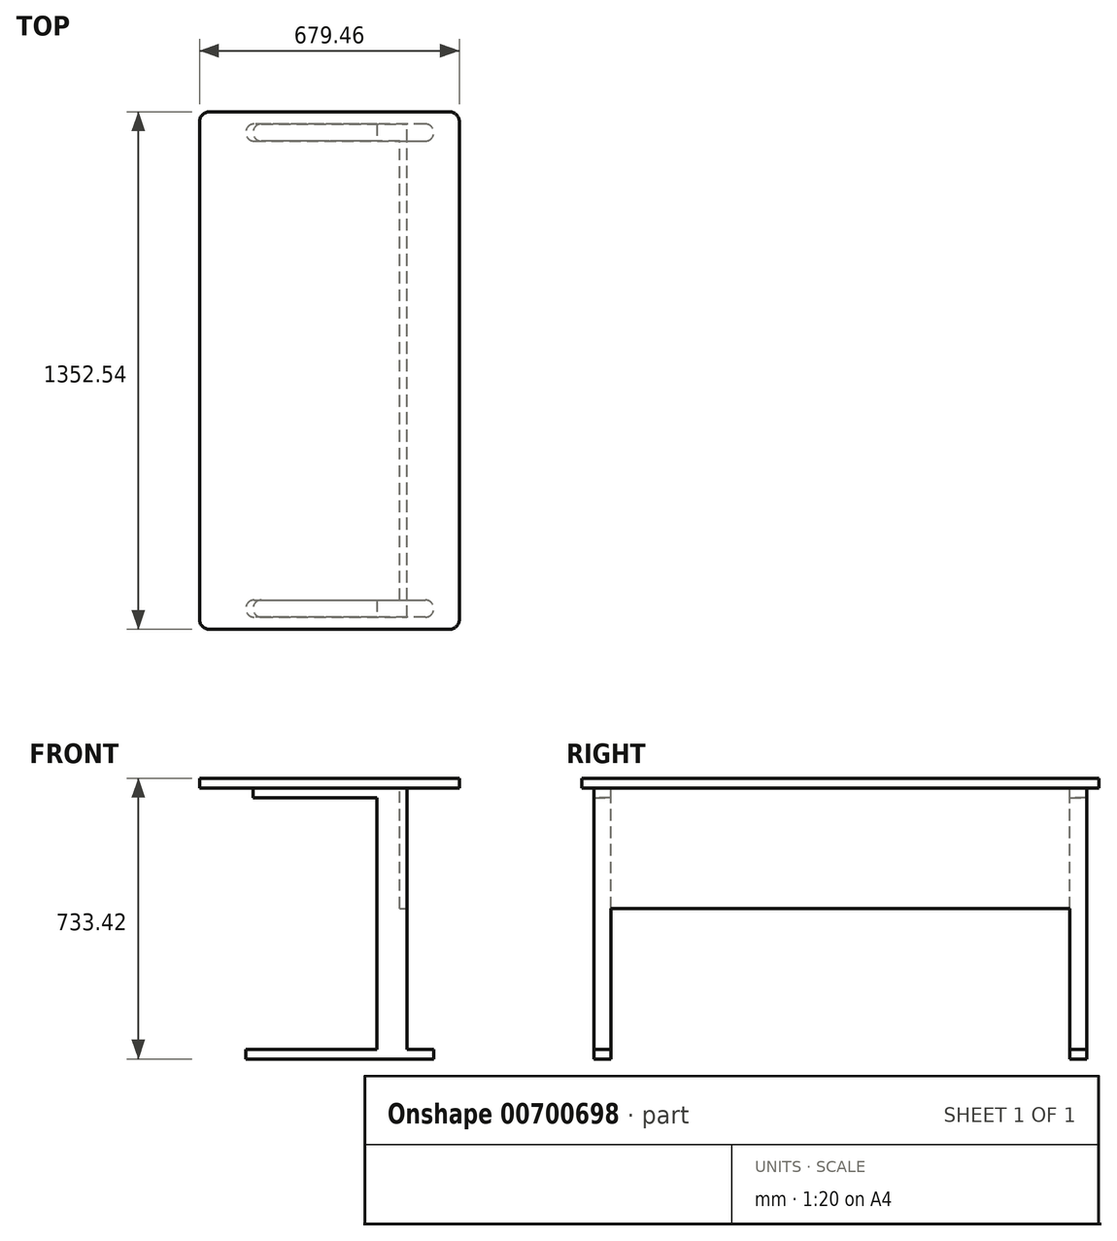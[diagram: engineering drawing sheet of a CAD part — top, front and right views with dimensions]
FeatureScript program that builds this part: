
annotation { "Feature Type Name" : "Feature", "Feature Type Description" : "" }
export const myFeature = defineFeature(function(context is Context, id is Id, definition is map)
    precondition{}
    {
        {
            var Q0;
            Q0=qCreatedBy(makeId("Top.planeOp"),FACE);
            var sketch = newSketch(context, id + "F0", { "sketchPlane" : qUnion([Q0])});
            skLineSegment(sketch, "E0.bottom", {"start": v(314.33, 676.28) * mm, "end": v(-314.32, 676.28) * mm});
            skLineSegment(sketch, "E0.top", {"start": v(314.32, -676.27) * mm, "end": v(-314.33, -676.27) * mm});
            skLineSegment(sketch, "E0.left", {"start": v(339.73, 650.88) * mm, "end": v(339.72, -650.88) * mm});
            skLineSegment(sketch, "E0.right", {"start": v(-339.72, 650.88) * mm, "end": v(-339.73, -650.88) * mm});
            skPoint(sketch, "E0.middle", {"position": v(0, 0) * mm});
            skPoint(sketch, "E1.visualSharp", {"position": v(339.73, 676.28) * mm});
            skArc(sketch, "E1.filletArc", {"start": v(339.73, 650.88) * mm, "mid": v(332.29, 668.84) * mm, "end": v(314.33, 676.28) * mm});
            skPoint(sketch, "E2.visualSharp", {"position": v(-339.72, 676.28) * mm});
            skArc(sketch, "E2.filletArc", {"start": v(-314.32, 676.28) * mm, "mid": v(-332.29, 668.84) * mm, "end": v(-339.72, 650.88) * mm});
            skPoint(sketch, "E3.visualSharp", {"position": v(-339.73, -676.27) * mm});
            skArc(sketch, "E3.filletArc", {"start": v(-339.73, -650.88) * mm, "mid": v(-332.29, -668.84) * mm, "end": v(-314.33, -676.27) * mm});
            skPoint(sketch, "E4.visualSharp", {"position": v(339.72, -676.27) * mm});
            skArc(sketch, "E4.filletArc", {"start": v(314.32, -676.27) * mm, "mid": v(332.29, -668.84) * mm, "end": v(339.72, -650.88) * mm});
            skSolve(sketch);
        }
        {
            var Q0;
            Q0 = qSketchRegion(id + "F0", true);
            extrude(context, id + "F1", {"entities" : qUnion([Q0]), "depth" : 25.4 * mm, "offsetDistance" : 25.4 * mm});
        }
        {
            var Q0;
            Q0=makeQuery(id+"F1.opExtrude","CAP_FACE",FACE,{"disambiguationData":[OSD([sQuery(id+"F0.wireOp",EDGE,"E0.bottom"),sQuery(id+"F0.wireOp",EDGE,"E0.top"),sQuery(id+"F0.wireOp",EDGE,"E0.left"),sQuery(id+"F0.wireOp",EDGE,"E0.right"),sQuery(id+"F0.wireOp",EDGE,"E1.filletArc"),sQuery(id+"F0.wireOp",EDGE,"E2.filletArc"),sQuery(id+"F0.wireOp",EDGE,"E3.filletArc"),sQuery(id+"F0.wireOp",EDGE,"E4.filletArc")])],"isStart":true});
            var sketch = newSketch(context, id + "F2", { "sketchPlane" : qUnion([Q0])});
            skLineSegment(sketch, "E5", {"start": v(-177.8, 600.08) * mm, "end": v(184.15, 600.08) * mm});
            skLineSegment(sketch, "E6", {"start": v(184.15, 600.08) * mm, "end": v(184.15, -600.08) * mm});
            skLineSegment(sketch, "E7", {"start": v(184.15, -600.07) * mm, "end": v(-177.8, -600.07) * mm});
            skArc(sketch, "E8", {"start": v(-177.8, -600.08) * mm, "mid": v(-200.03, -622.3) * mm, "end": v(-177.8, -644.53) * mm});
            skArc(sketch, "E9", {"start": v(-177.8, 600.08) * mm, "mid": v(-200.03, 622.3) * mm, "end": v(-177.8, 644.53) * mm});
            skLineSegment(sketch, "E10", {"start": v(-177.8, 644.52) * mm, "end": v(203.2, 644.52) * mm});
            skLineSegment(sketch, "E11", {"start": v(203.2, 644.52) * mm, "end": v(203.2, -644.52) * mm});
            skLineSegment(sketch, "E12", {"start": v(-177.8, -644.53) * mm, "end": v(203.2, -644.53) * mm});
            skSolve(sketch);
        }
        {
            var Q0;
            Q0 = qSketchRegion(id + "F2", true);
            extrude(context, id + "F3", {"entities" : qUnion([Q0]), "operationType" : NewBodyOperationType.ADD, "depth" : 25.4 * mm, "offsetDistance" : 25.4 * mm});
        }
        {
            var Q0;
            Q0=makeQuery(id+"F3.opExtrude","CAP_FACE",FACE,{"disambiguationData":[OSD([sQuery(id+"F2.wireOp",EDGE,"E5"),sQuery(id+"F2.wireOp",EDGE,"E6"),sQuery(id+"F2.wireOp",EDGE,"E7"),sQuery(id+"F2.wireOp",EDGE,"E8"),sQuery(id+"F2.wireOp",EDGE,"E9"),sQuery(id+"F2.wireOp",EDGE,"E10"),sQuery(id+"F2.wireOp",EDGE,"E11"),sQuery(id+"F2.wireOp",EDGE,"E12")])],"isStart":false});
            var sketch = newSketch(context, id + "F4", { "sketchPlane" : qUnion([Q0])});
            skLineSegment(sketch, "E13", {"start": v(123.83, 600.08) * mm, "end": v(123.83, 644.52) * mm});
            skLineSegment(sketch, "E14", {"start": v(123.83, 644.52) * mm, "end": v(203.2, 644.52) * mm});
            skLineSegment(sketch, "E15", {"start": v(203.2, 644.52) * mm, "end": v(203.2, -644.52) * mm});
            skLineSegment(sketch, "E16", {"start": v(203.2, -644.52) * mm, "end": v(123.83, -644.53) * mm});
            skLineSegment(sketch, "E17", {"start": v(123.83, -644.53) * mm, "end": v(123.83, -600.08) * mm});
            skLineSegment(sketch, "E18", {"start": v(123.83, -600.08) * mm, "end": v(184.15, -600.08) * mm});
            skLineSegment(sketch, "E19", {"start": v(184.15, -600.08) * mm, "end": v(184.15, 600.08) * mm});
            skLineSegment(sketch, "E20", {"start": v(184.15, 600.08) * mm, "end": v(123.83, 600.08) * mm});
            skSolve(sketch);
        }
        {
            var Q0;
            Q0 = qSketchRegion(id + "F4", true);
            extrude(context, id + "F5", {"entities" : qUnion([Q0]), "operationType" : NewBodyOperationType.ADD, "depth" : 288.93 * mm, "offsetDistance" : 25.4 * mm});
        }
        {
            var Q0;
            Q0=makeQuery(id+"F5.opExtrude","CAP_FACE",FACE,{"disambiguationData":[OSD([sQuery(id+"F4.wireOp",EDGE,"E13"),sQuery(id+"F4.wireOp",EDGE,"E14"),sQuery(id+"F4.wireOp",EDGE,"E15"),sQuery(id+"F4.wireOp",EDGE,"E16"),sQuery(id+"F4.wireOp",EDGE,"E17"),sQuery(id+"F4.wireOp",EDGE,"E18"),sQuery(id+"F4.wireOp",EDGE,"E19"),sQuery(id+"F4.wireOp",EDGE,"E20")])],"isStart":false});
            var sketch = newSketch(context, id + "F6", { "sketchPlane" : qUnion([Q0])});
            skLineSegment(sketch, "E21.bottom", {"start": v(123.83, -644.53) * mm, "end": v(203.2, -644.53) * mm});
            skLineSegment(sketch, "E21.top", {"start": v(123.83, -600.08) * mm, "end": v(203.2, -600.08) * mm});
            skLineSegment(sketch, "E21.left", {"start": v(123.83, -644.53) * mm, "end": v(123.83, -600.08) * mm});
            skLineSegment(sketch, "E21.right", {"start": v(203.2, -644.53) * mm, "end": v(203.2, -600.08) * mm});
            skLineSegment(sketch, "E22.bottom", {"start": v(123.83, 644.52) * mm, "end": v(203.2, 644.52) * mm});
            skLineSegment(sketch, "E22.top", {"start": v(123.83, 600.08) * mm, "end": v(203.2, 600.08) * mm});
            skLineSegment(sketch, "E22.left", {"start": v(123.83, 644.52) * mm, "end": v(123.83, 600.08) * mm});
            skLineSegment(sketch, "E22.right", {"start": v(203.2, 644.52) * mm, "end": v(203.2, 600.08) * mm});
            skSolve(sketch);
        }
        {
            var Q0;
            Q0 = qSketchRegion(id + "F6", true);
            extrude(context, id + "F7", {"entities" : qUnion([Q0]), "operationType" : NewBodyOperationType.ADD, "depth" : 368.3 * mm, "offsetDistance" : 25.4 * mm});
        }
        {
            var Q0;
            Q0=makeQuery(id+"F7.opExtrude","CAP_FACE",FACE,{"disambiguationData":[OSD([sQuery(id+"F6.wireOp",EDGE,"E22.bottom"),sQuery(id+"F6.wireOp",EDGE,"E22.top"),sQuery(id+"F6.wireOp",EDGE,"E22.left"),sQuery(id+"F6.wireOp",EDGE,"E22.right")])],"isStart":false});
            var sketch = newSketch(context, id + "F8", { "sketchPlane" : qUnion([Q0])});
            skLineSegment(sketch, "E23", {"start": v(250.82, 644.52) * mm, "end": v(-196.85, 644.52) * mm});
            skArc(sketch, "E24", {"start": v(-196.85, 644.53) * mm, "mid": v(-219.08, 622.3) * mm, "end": v(-196.85, 600.08) * mm});
            skArc(sketch, "E25", {"start": v(250.82, 644.52) * mm, "mid": v(273.05, 622.3) * mm, "end": v(250.82, 600.08) * mm});
            skLineSegment(sketch, "E26", {"start": v(-196.85, 600.08) * mm, "end": v(250.82, 600.08) * mm});
            skLineSegment(sketch, "E27.MirrorCS", {"start": v(-196.85, -600.08) * mm, "end": v(250.82, -600.08) * mm});
            skArc(sketch, "E28.MirrorCS", {"start": v(250.82, -644.52) * mm, "mid": v(273.05, -622.3) * mm, "end": v(250.82, -600.08) * mm});
            skLineSegment(sketch, "E29.MirrorCS", {"start": v(250.82, -644.52) * mm, "end": v(-196.85, -644.52) * mm});
            skArc(sketch, "E30.MirrorCS", {"start": v(-196.85, -644.53) * mm, "mid": v(-219.08, -622.3) * mm, "end": v(-196.85, -600.08) * mm});
            skSolve(sketch);
        }
        {
            var Q0;
            Q0 = qSketchRegion(id + "F8", true);
            extrude(context, id + "F9", {"entities" : qUnion([Q0]), "operationType" : NewBodyOperationType.ADD, "depth" : 25.4 * mm, "offsetDistance" : 25.4 * mm});
        }
    });
